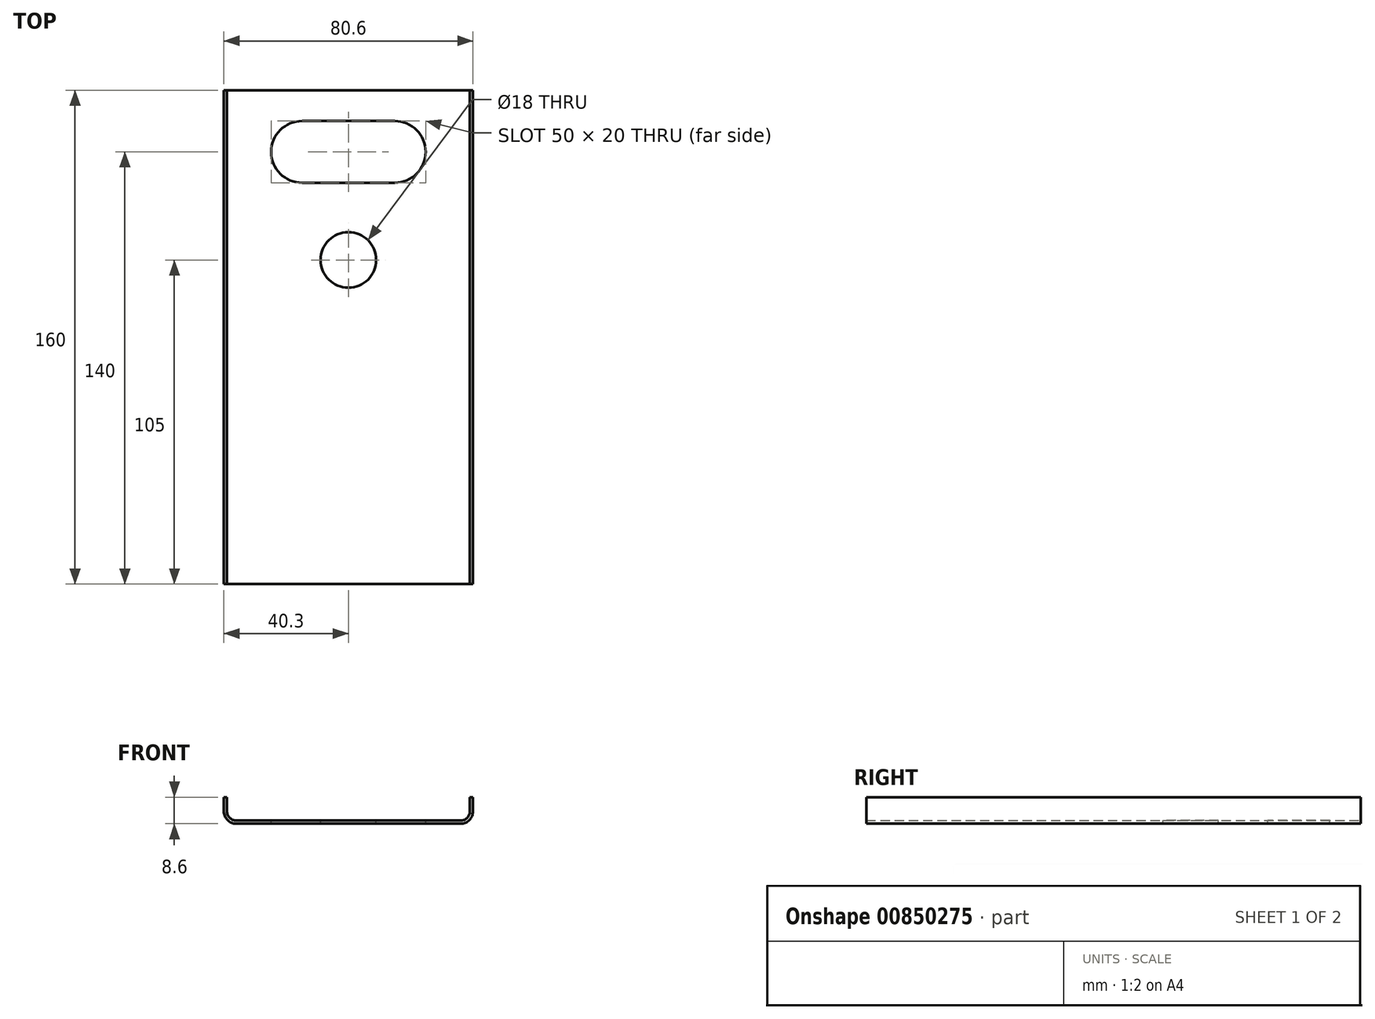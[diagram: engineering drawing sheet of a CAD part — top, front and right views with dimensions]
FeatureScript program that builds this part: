
annotation { "Feature Type Name" : "Feature", "Feature Type Description" : "" }
export const myFeature = defineFeature(function(context is Context, id is Id, definition is map)
    precondition{}
    {
        {
            var Q0;
            Q0=qCreatedBy(makeId("Front.planeOp"),FACE);
            var sketch = newSketch(context, id + "F0", { "sketchPlane" : qUnion([Q0])});
            skLineSegment(sketch, "E0", {"start": v(-36.3, 0) * mm, "end": v(36.3, 0) * mm});
            skLineSegment(sketch, "E1", {"start": v(39.3, 3) * mm, "end": v(39.3, 7.6) * mm});
            skLineSegment(sketch, "E2", {"start": v(-39.3, 3) * mm, "end": v(-39.3, 7.6) * mm});
            skPoint(sketch, "E3.visualSharp", {"position": v(-39.3, 0) * mm});
            skArc(sketch, "E3.filletArc", {"start": v(-39.3, 3) * mm, "mid": v(-38.42, 0.88) * mm, "end": v(-36.3, 0) * mm});
            skPoint(sketch, "E4.visualSharp", {"position": v(39.3, 0) * mm});
            skArc(sketch, "E4.filletArc", {"start": v(36.3, 0) * mm, "mid": v(38.42, 0.88) * mm, "end": v(39.3, 3) * mm});
            skLineSegment(sketch, "E5.0", {"start": v(-40.3, 3) * mm, "end": v(-40.3, 7.6) * mm});
            skLineSegment(sketch, "E5.1", {"start": v(40.3, 3) * mm, "end": v(40.3, 7.6) * mm});
            skArc(sketch, "E5.2", {"start": v(36.3, -1) * mm, "mid": v(39.13, 0.17) * mm, "end": v(40.3, 3) * mm});
            skLineSegment(sketch, "E5.3", {"start": v(-36.3, -1) * mm, "end": v(36.3, -1) * mm});
            skArc(sketch, "E5.4", {"start": v(-40.3, 3) * mm, "mid": v(-39.13, 0.17) * mm, "end": v(-36.3, -1) * mm});
            skLineSegment(sketch, "E6", {"start": v(-40.3, 7.6) * mm, "end": v(-39.3, 7.6) * mm});
            skLineSegment(sketch, "E7", {"start": v(40.3, 7.6) * mm, "end": v(39.3, 7.6) * mm});
            skSolve(sketch);
        }
        {
            var Q0;
            Q0=makeQuery(id+"F0.imprint","IMPRINT",FACE,{"disambiguationData":[TD([[makeQuery(id+"F0.imprint","IMPRINT",EDGE,{"derivedFrom":sQuery(id+"F0.wireOp",EDGE,"E0")}),-1.0]])]});
            extrude(context, id + "F1", {"entities" : qUnion([Q0]), "endBound" : BoundingType.SYMMETRIC, "depth" : 160 * mm, "offsetDistance" : 25 * mm});
        }
        {
            var Q0;
            Q0=qCreatedBy(makeId("Top.planeOp"),FACE);
            var sketch = newSketch(context, id + "F2", { "sketchPlane" : qUnion([Q0])});
            skLineSegment(sketch, "E8.bottom", {"start": v(15, 70) * mm, "end": v(-15, 70) * mm});
            skLineSegment(sketch, "E8.top", {"start": v(15, 50) * mm, "end": v(-15, 50) * mm});
            skLineSegment(sketch, "E8.left", {"start": v(15, 70) * mm, "end": v(15, 50) * mm});
            skLineSegment(sketch, "E8.right", {"start": v(-15, 70) * mm, "end": v(-15, 50) * mm});
            skPoint(sketch, "E8.middle", {"position": v(0, 60) * mm});
            skCircle(sketch, "E9", {"center": v(0, 25) * mm, "radius": 9 * mm});
            skCircle(sketch, "E10", {"center": v(15, 60) * mm, "radius": 10 * mm});
            skCircle(sketch, "E11", {"center": v(-15, 60) * mm, "radius": 10 * mm});
            skSolve(sketch);
        }
        {
            var Q0;
            {var subQ0=sQuery(id+"F2.wireOp",EDGE,"E8.right");Q0=makeQuery(id+"F2.imprint","IMPRINT",FACE,{"disambiguationData":[TD([[makeQuery(id+"F2.imprint","IMPRINT",EDGE,{"derivedFrom":subQ0}),-1.0]])]});}
            var Q1;
            {var subQ0=sQuery(id+"F2.wireOp",EDGE,"E8.right");Q1=makeQuery(id+"F2.imprint","IMPRINT",FACE,{"disambiguationData":[TD([[makeQuery(id+"F2.imprint","IMPRINT",EDGE,{"derivedFrom":subQ0}),1.0]])]});}
            var Q2;
            {var subQ0=sQuery(id+"F2.wireOp",EDGE,"E8.bottom");Q2=makeQuery(id+"F2.imprint","IMPRINT",FACE,{"disambiguationData":[TD([[makeQuery(id+"F2.imprint","IMPRINT",EDGE,{"derivedFrom":subQ0}),1.0]])]});}
            var Q3;
            {var subQ0=sQuery(id+"F2.wireOp",EDGE,"E8.left");Q3=makeQuery(id+"F2.imprint","IMPRINT",FACE,{"disambiguationData":[TD([[makeQuery(id+"F2.imprint","IMPRINT",EDGE,{"derivedFrom":subQ0}),-1.0]])]});}
            var Q4;
            {var subQ0=sQuery(id+"F2.wireOp",EDGE,"E8.left");Q4=makeQuery(id+"F2.imprint","IMPRINT",FACE,{"disambiguationData":[TD([[makeQuery(id+"F2.imprint","IMPRINT",EDGE,{"derivedFrom":subQ0}),1.0]])]});}
            var Q5;
            Q5=makeQuery(id+"F2.imprint","IMPRINT",FACE,{"disambiguationData":[TD([[makeQuery(id+"F2.imprint","IMPRINT",EDGE,{"derivedFrom":sQuery(id+"F2.wireOp",EDGE,"E9")}),1.0]])]});
            extrude(context, id + "F3", {"entities" : qUnion([Q0, Q1, Q2, Q3, Q4, Q5]), "operationType" : NewBodyOperationType.REMOVE, "endBound" : BoundingType.SYMMETRIC, "oppositeDirection" : true, "depth" : 25 * mm, "offsetDistance" : 25 * mm});
        }
    });
